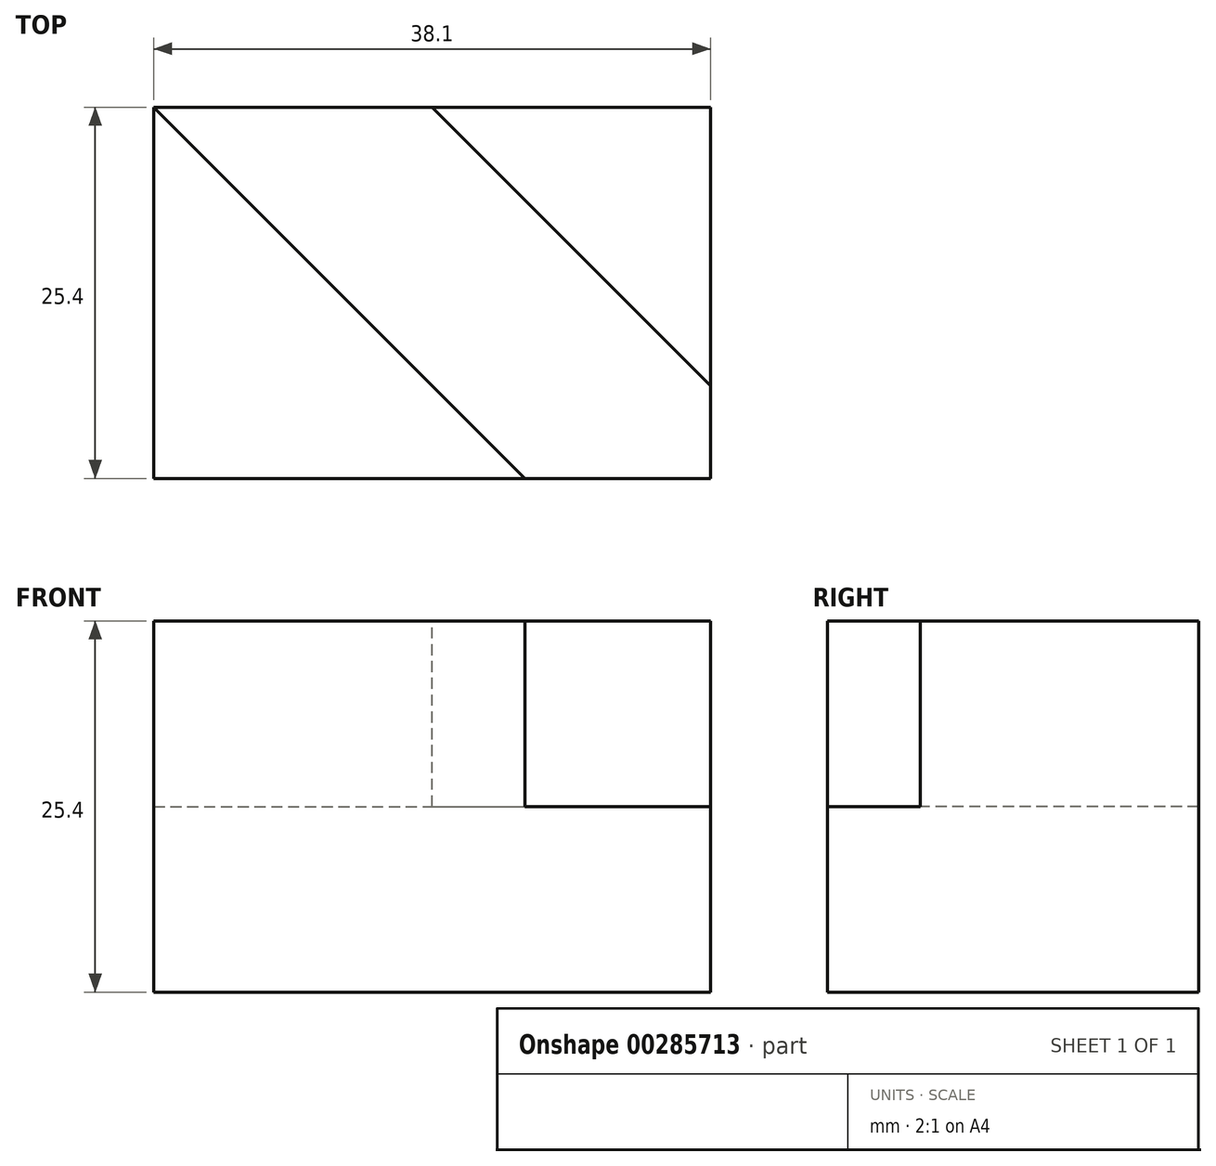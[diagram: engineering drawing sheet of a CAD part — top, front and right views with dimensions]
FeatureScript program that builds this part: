
annotation { "Feature Type Name" : "Feature", "Feature Type Description" : "" }
export const myFeature = defineFeature(function(context is Context, id is Id, definition is map)
    precondition{}
    {
        {
            var Q0;
            Q0=qCreatedBy(makeId("Top.planeOp"),FACE);
            var sketch = newSketch(context, id + "F0", { "sketchPlane" : qUnion([Q0])});
            skLineSegment(sketch, "E0.bottom", {"start": v(0, 0) * mm, "end": v(38.1, 0) * mm});
            skLineSegment(sketch, "E0.top", {"start": v(0, 25.4) * mm, "end": v(38.1, 25.4) * mm});
            skLineSegment(sketch, "E0.left", {"start": v(0, 0) * mm, "end": v(0, 25.4) * mm});
            skLineSegment(sketch, "E0.right", {"start": v(38.1, 0) * mm, "end": v(38.1, 25.4) * mm});
            skSolve(sketch);
        }
        {
            var Q0;
            Q0 = qSketchRegion(id + "F0", true);
            extrude(context, id + "F1", {"entities" : qUnion([Q0]), "depth" : 25.4 * mm});
        }
        {
            var Q0;
            Q0=makeQuery(id+"F1.opExtrude","CAP_FACE",FACE,{"disambiguationData":[OSD([sQuery(id+"F0.wireOp",EDGE,"E0.bottom"),sQuery(id+"F0.wireOp",EDGE,"E0.top"),sQuery(id+"F0.wireOp",EDGE,"E0.left"),sQuery(id+"F0.wireOp",EDGE,"E0.right")])],"isStart":false});
            var sketch = newSketch(context, id + "F2", { "sketchPlane" : qUnion([Q0])});
            skLineSegment(sketch, "E1", {"start": v(0, 25.4) * mm, "end": v(25.4, 0) * mm});
            skLineSegment(sketch, "E2", {"start": v(19.05, 25.4) * mm, "end": v(38.1, 6.35) * mm});
            skLineSegment(sketch, "E3", {"start": v(0, 25.4) * mm, "end": v(19.05, 25.4) * mm});
            skLineSegment(sketch, "E4", {"start": v(25.4, 0) * mm, "end": v(38.1, 0) * mm});
            skLineSegment(sketch, "E5", {"start": v(38.1, 6.35) * mm, "end": v(38.1, 0) * mm});
            skSolve(sketch);
        }
        {
            var Q0;
            Q0 = qSketchRegion(id + "F2", true);
            extrude(context, id + "F3", {"entities" : qUnion([Q0]), "operationType" : NewBodyOperationType.REMOVE, "oppositeDirection" : true, "depth" : 12.7 * mm});
        }
    });
